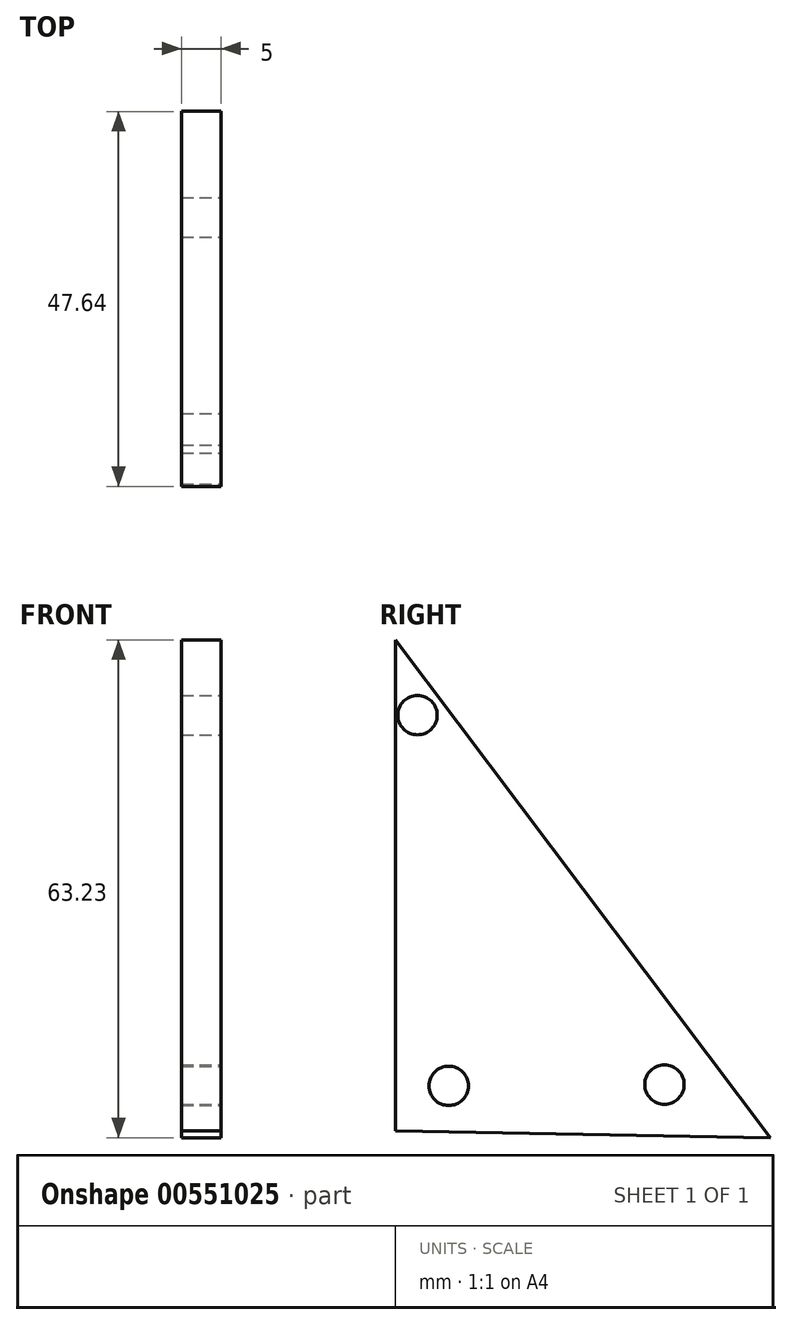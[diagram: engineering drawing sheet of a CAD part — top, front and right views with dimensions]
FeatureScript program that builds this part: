
annotation { "Feature Type Name" : "Feature", "Feature Type Description" : "" }
export const myFeature = defineFeature(function(context is Context, id is Id, definition is map)
    precondition{}
    {
        {
            var Q0;
            Q0=qCreatedBy(makeId("Right.planeOp"),FACE);
            var sketch = newSketch(context, id + "F0", { "sketchPlane" : qUnion([Q0])});
            skLineSegment(sketch, "E0", {"start": v(-22.94, 40) * mm, "end": v(-22.94, -22.33) * mm});
            skLineSegment(sketch, "E1", {"start": v(-22.94, -22.33) * mm, "end": v(24.7, -23.22) * mm});
            skLineSegment(sketch, "E2", {"start": v(24.7, -23.22) * mm, "end": v(24.7, -23.22) * mm});
            skLineSegment(sketch, "E3", {"start": v(24.7, -23.22) * mm, "end": v(-22.94, 40) * mm});
            skSolve(sketch);
        }
        {
            var Q0;
            Q0=makeQuery(id+"F0.imprint","IMPRINT",FACE,{"disambiguationData":[TD([[makeQuery(id+"F0.imprint","IMPRINT",EDGE,{"derivedFrom":sQuery(id+"F0.wireOp",EDGE,"E0")}),1.0]])]});
            extrude(context, id + "F1", {"entities" : qUnion([Q0]), "depth" : 5 * mm, "offsetDistance" : 25 * mm});
        }
        {
            var Q0;
            Q0=makeQuery(id+"F1.opExtrude","CAP_FACE",FACE,{"disambiguationData":[OSD([sQuery(id+"F0.wireOp",EDGE,"E0"),sQuery(id+"F0.wireOp",EDGE,"E1"),sQuery(id+"F0.wireOp",EDGE,"E3")])],"isStart":false});
            var sketch = newSketch(context, id + "F2", { "sketchPlane" : qUnion([Q0])});
            skCircle(sketch, "E4", {"center": v(11.22, -16.48) * mm, "radius": 5.1 * mm, "construction": true});
            skCircle(sketch, "E5", {"center": v(0, 0) * mm, "radius": 5.1 * mm, "construction": true});
            skSolve(sketch);
        }
        {
            var Q0;
            Q0=sQuery(id+"F2.wireOp",VERTEX,"E4.center");
            var Q1;
            Q1=makeQuery(id+"F1.opExtrude","SWEPT_BODY",BODY,{"disambiguationData":[OSD([sQuery(id+"F0.wireOp",EDGE,"E0"),sQuery(id+"F0.wireOp",EDGE,"E1"),sQuery(id+"F0.wireOp",EDGE,"E3")])]});
            hole(context, id + "F3", {"style" : HoleStyle.SIMPLE, "endStyle" : HoleEndStyle.THROUGH, "holeDiameter" : 5 * mm, "isTappedThrough" : true, "tappedDepth" : 12 * mm, "tapClearance" : 3, "locations" : qUnion([Q0]), "scope" : qUnion([Q1])});
        }
        {
            var Q0;
            Q0=makeQuery(id+"F1.opExtrude","CAP_FACE",FACE,{"disambiguationData":[OSD([sQuery(id+"F0.wireOp",EDGE,"E0"),sQuery(id+"F0.wireOp",EDGE,"E1"),sQuery(id+"F0.wireOp",EDGE,"E3")])],"isStart":false});
            var sketch = newSketch(context, id + "F4", { "sketchPlane" : qUnion([Q0])});
            skCircle(sketch, "E6", {"center": v(-16.19, -16.64) * mm, "radius": 1.27 * mm});
            skSolve(sketch);
        }
        {
            var Q0;
            Q0=sQuery(id+"F4.wireOp",VERTEX,"E6.center");
            var Q1;
            Q1=makeQuery(id+"F1.opExtrude","SWEPT_BODY",BODY,{"disambiguationData":[OSD([sQuery(id+"F0.wireOp",EDGE,"E0"),sQuery(id+"F0.wireOp",EDGE,"E1"),sQuery(id+"F0.wireOp",EDGE,"E3")])]});
            hole(context, id + "F5", {"style" : HoleStyle.SIMPLE, "endStyle" : HoleEndStyle.THROUGH, "holeDiameter" : 5 * mm, "isTappedThrough" : true, "tappedDepth" : 12 * mm, "tapClearance" : 3, "locations" : qUnion([Q0]), "scope" : qUnion([Q1])});
        }
        {
            var Q0;
            Q0=makeQuery(id+"F1.opExtrude","CAP_FACE",FACE,{"disambiguationData":[OSD([sQuery(id+"F0.wireOp",EDGE,"E0"),sQuery(id+"F0.wireOp",EDGE,"E1"),sQuery(id+"F0.wireOp",EDGE,"E3")])],"isStart":false});
            var sketch = newSketch(context, id + "F6", { "sketchPlane" : qUnion([Q0])});
            skCircle(sketch, "E7", {"center": v(-20.15, 30.46) * mm, "radius": 1.94 * mm});
            skSolve(sketch);
        }
        {
            var Q0;
            Q0=sQuery(id+"F6.wireOp",VERTEX,"E7.center");
            var Q1;
            Q1=makeQuery(id+"F1.opExtrude","SWEPT_BODY",BODY,{"disambiguationData":[OSD([sQuery(id+"F0.wireOp",EDGE,"E0"),sQuery(id+"F0.wireOp",EDGE,"E1"),sQuery(id+"F0.wireOp",EDGE,"E3")])]});
            hole(context, id + "F7", {"style" : HoleStyle.SIMPLE, "endStyle" : HoleEndStyle.THROUGH, "holeDiameter" : 5 * mm, "isTappedThrough" : true, "tappedDepth" : 12 * mm, "tapClearance" : 3, "locations" : qUnion([Q0]), "scope" : qUnion([Q1])});
        }
    });
